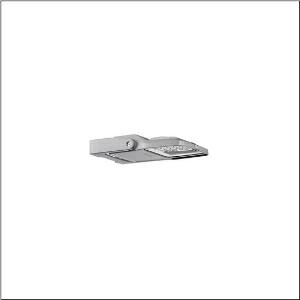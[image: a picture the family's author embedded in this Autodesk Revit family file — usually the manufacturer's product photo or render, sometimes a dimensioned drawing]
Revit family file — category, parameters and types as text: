
# Revit family: floodlight_fl_21_iq_micro___pl52_5xa7761a2d2a_1372
name_source: partatom
category: Lighting Fixtures
units: mm (PartAtom-declared; Revit-internal decimal feet)

## family parameters
Cut with Voids When Loaded = No
Host = Face
Light Source = No
Part Type = Normal
Room Calculation Point = No
Round Connector Dimension = Use Diameter
Shared = No

## types (1)
- --- (1 x LED, 2890 lm, 23.1 W, 3000K)
    Apparent Load = 23 VA
    CIE Flux Codes = 26 60 98 100 100
    Color Rendering = 70
    Color Temperature = 3000K
    Default Elevation = 1800 mm
    Description = Floodlight FL 21 iQ micro, floodlight, primary light control with lens, of PMMA, primary optical cover: protective disc, of toughened safety glass, transparent, light distribution: PL52, light emission: direct distribution, installation type: surface-mounted, LED, High Power LED, rated luminous flux: 2.890lm, luminous efficacy: 125lm/W, light colour: 730, colour temperature: 3000K, control: optimised constant luminous flux control (CLO 2.0), Desk-Remote (wireless, voltage-free reading and setting of iQ features in the workshop via application-optimized NFC function/RFID function), Light-Fading, Smart-Wire, Night-Set, Lumen-Switch, Temp-Guard, Auto-Match, with terminal, 6-pole, mains connection: 220..240V, AC, 50/60Hz, start of lifetime: 23W, end of service life: 24W, reduction: 11W, luminaire housing, of diecast aluminium, powder-coated, Siteco® metallic grey (DB 702S), corrosivity category C5 mid according to DIN EN ISO 12944, sealing non-destructively replaceable, design bracket, of diecast aluminium, powder-coated, Siteco® metallic grey (DB 702S), protection rating (complete): IP66, insulation class (complete): insulation class II (safety insulation), certification: CE, ENEC, VDE, protection symbol: D, impact resistance: IK07, permissible operating ambient temperature: -40..+40°C, permissible operating ambient temperature for outdoor applications: -40..+50°C, standard: DIN EN 12944, LABS conformity tested according to VDMA 24364:2018-05, packaging unit: 1 piece

Light Distribution: PL52
    Height = 65 mm
    Lamp = 1 x LED
    Lamp Light Flux = 2890 lm
    Lamp Power = 23.1 W
    Lamp count = 1
    Length = 312 mm
    Luminous efficacy = 125 lm/W
    Manufacturer = Siteco
    ModVariant = No
    Model = 5XA7761A2D2A
    Mounting Place = Wall
    Mounting Type = Surface mounted
    Number of Poles = 1
    OnlyDefault = Yes
    Power Factor = 1
    Product Name = Floodlight FL 21 iQ micro | PL52
    Product group = floodlight | wall mounted
    ProductGroupID = 2001
    Protection Class = Protection class II
    Protection Degree = IP 66
    RLX_Detail_Level = 1
    RLX_Emergency_Light_Flux = 0 lm
    RLX_Emergency_Type = 0
    RLX_Emergency_Type_DB = No
    RlxData = <blob elided: 97533 chars, md5=cd18a4cc>
    Socket = socket
    Standby Power = 0 W
    System Light Flux = 2890 lm
    System Power = 23 W
    Type Comments = factory setting: luminous flux: 100 % | dim-lin: 254 | 455 mA
    Type Image = l_1006878.jpg
    URL = http://relux.com
    VarID = @adj_129319
    Voltage = 0 V
    Weight = 0.00 kg
    Width = 230 mm

## geometry (parser evidence)
native form markers: Blend x4, Sweep x13
no freeform markers — native parametric forms only
